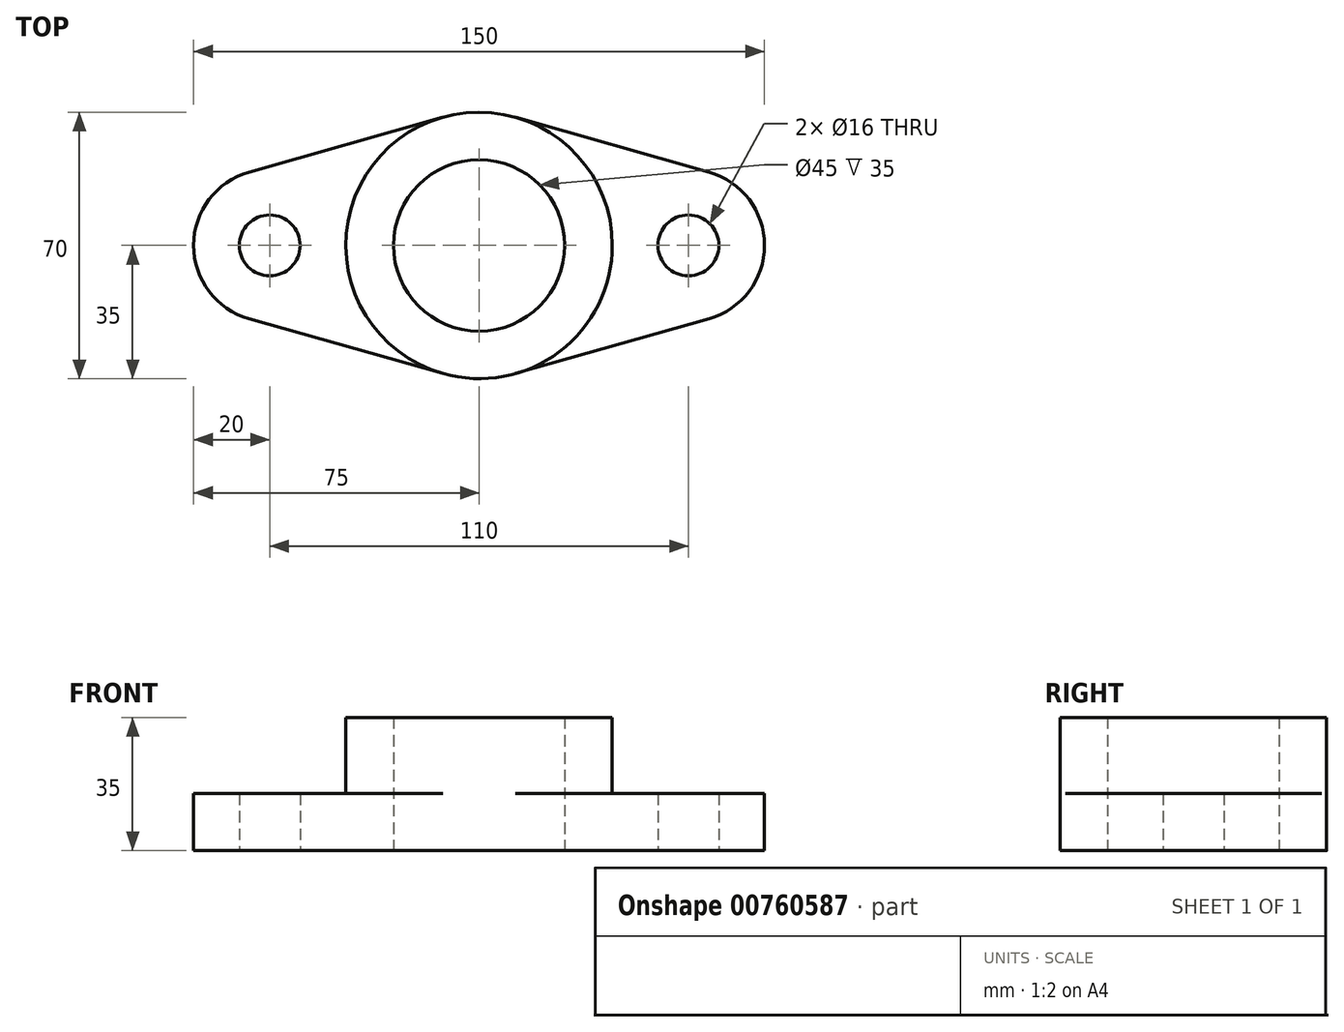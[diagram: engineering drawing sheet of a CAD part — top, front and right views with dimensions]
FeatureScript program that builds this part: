
annotation { "Feature Type Name" : "Feature", "Feature Type Description" : "" }
export const myFeature = defineFeature(function(context is Context, id is Id, definition is map)
    precondition{}
    {
        {
            var Q0;
            Q0=qCreatedBy(makeId("Top.planeOp"),FACE);
            var sketch = newSketch(context, id + "F0", { "sketchPlane" : qUnion([Q0])});
            skCircle(sketch, "E0", {"center": v(0, 0) * mm, "radius": 22.5 * mm});
            skCircle(sketch, "E1", {"center": v(0, 0) * mm, "radius": 35 * mm});
            skCircle(sketch, "E2", {"center": v(55, 0) * mm, "radius": 8 * mm});
            skArc(sketch, "E3", {"start": v(60.45, -19.24) * mm, "mid": v(75, 0) * mm, "end": v(60.45, 19.24) * mm});
            skCircle(sketch, "E4", {"center": v(-55, 0) * mm, "radius": 8 * mm});
            skArc(sketch, "E5", {"start": v(-60.45, 19.24) * mm, "mid": v(-75, 0) * mm, "end": v(-60.45, -19.24) * mm});
            skLineSegment(sketch, "E6", {"start": v(9.55, 33.67) * mm, "end": v(60.45, 19.24) * mm});
            skLineSegment(sketch, "E7", {"start": v(-9.55, 33.67) * mm, "end": v(-60.45, 19.24) * mm});
            skLineSegment(sketch, "E8", {"start": v(-60.45, -19.24) * mm, "end": v(-9.55, -33.67) * mm});
            skLineSegment(sketch, "E9", {"start": v(9.55, -33.67) * mm, "end": v(60.45, -19.24) * mm});
            skSolve(sketch);
        }
        {
            var Q0;
            Q0=makeQuery(id+"F0.imprint","IMPRINT",FACE,{"disambiguationData":[TD([[makeQuery(id+"F0.imprint","IMPRINT",EDGE,{"derivedFrom":sQuery(id+"F0.wireOp",EDGE,"E0")}),-1.0]])]});
            var Q1;
            Q1=makeQuery(id+"F0.imprint","IMPRINT",FACE,{"disambiguationData":[TD([[makeQuery(id+"F0.imprint","IMPRINT",EDGE,{"derivedFrom":sQuery(id+"F0.wireOp",EDGE,"E2")}),-1.0]])]});
            var Q2;
            Q2=makeQuery(id+"F0.imprint","IMPRINT",FACE,{"disambiguationData":[TD([[makeQuery(id+"F0.imprint","IMPRINT",EDGE,{"derivedFrom":sQuery(id+"F0.wireOp",EDGE,"E4")}),-1.0]])]});
            extrude(context, id + "F1", {"entities" : qUnion([Q0, Q1, Q2]), "depth" : 15 * mm, "offsetDistance" : 25 * mm});
        }
        {
            var Q0;
            Q0=qCreatedBy(makeId("Top.planeOp"),FACE);
            var sketch = newSketch(context, id + "F2", { "sketchPlane" : qUnion([Q0])});
            skCircle(sketch, "E10", {"center": v(0, 0) * mm, "radius": 35 * mm});
            skCircle(sketch, "E11", {"center": v(0, 0) * mm, "radius": 22.5 * mm});
            skSolve(sketch);
        }
        {
            var Q0;
            Q0 = qSketchRegion(id + "F2", true);
            extrude(context, id + "F3", {"entities" : qUnion([Q0]), "operationType" : NewBodyOperationType.ADD, "depth" : 35 * mm, "offsetDistance" : 25 * mm});
        }
    });
